# Revit family: SCLT-CM
name_source: partatom
category: Lighting Fixtures
units: mm (PartAtom-declared; Revit-internal decimal feet)

## family parameters
Cut with Voids When Loaded = No
Host = Face
Light Source = Yes
OmniClass Number = 23.80.70.11.14
OmniClass Title = General Luminaries, Directional
Part Type = Normal
Room Calculation Point = No
Round Connector Dimension = Use Diameter
Shared = No

## types (3) — shared parameters
Cable Height = 24"
Color Filter = 16777215
Default Elevation = 48"
Description = LED Troffer with Advanced Solid State Technology
Dimming Lamp Color Temperature Shift = Incandescent Lamp Curve
Emit Shape Visible in Rendering = No
Finish = Arctic White
Glass = White Glass
Lamp = LED
Load Classification = Lighting
Manufacturer = Columbia Lighting
Model = SCLT
Photometric Notes = More IES files download Photometric Web Link
Photometric Web File = generic.ies
Power Factor = 1
Tilt Angle = 90.00°
URL = https://www.currentlighting.com
Voltage = 120 V
Warranty = 5 Years Limited Warranty

## per-type parameters (varying)
| type | Apparent Load | Emit from Rectangle Length | Emit from Rectangle Width | Size Option | Wattage Comments | Watts | zz Width 1 |
| SCLT-24 | 38 VA | 47" | 23" | SCLT : 24 | 34W | 38 W | 48" |
| SCLT-22 | 38 VA | 23" | 23" | SCLT : 22 | 28W | 38 W | 24" |
| SCLT-14 | 45 VA | 47" | 11" | SCLT : 14 | 45W | 45 W | 48" |

## geometry (parser evidence)
native form markers: Blend x3, Sweep x5
no freeform markers — native parametric forms only
